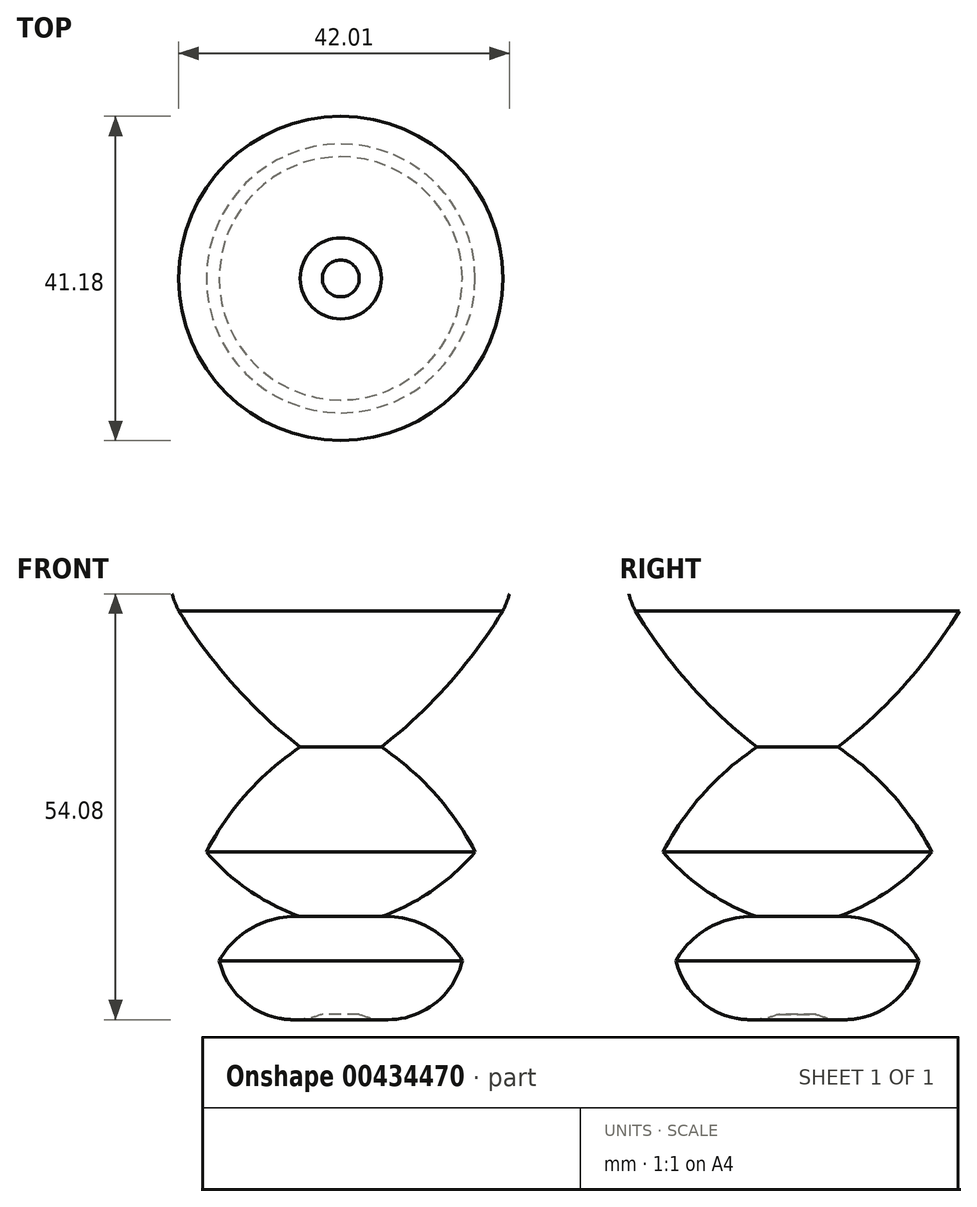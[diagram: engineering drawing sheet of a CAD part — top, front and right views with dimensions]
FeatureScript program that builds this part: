
annotation { "Feature Type Name" : "Feature", "Feature Type Description" : "" }
export const myFeature = defineFeature(function(context is Context, id is Id, definition is map)
    precondition{}
    {
        {
            var Q0;
            Q0=qCreatedBy(makeId("Front.planeOp"),FACE);
            var sketch = newSketch(context, id + "F0", { "sketchPlane" : qUnion([Q0])});
            skLineSegment(sketch, "E0", {"start": v(0, 0) * mm, "end": v(0, 68.09) * mm});
            skSolve(sketch);
        }
        {
            var Q0;
            Q0=qCreatedBy(makeId("Front.planeOp"),FACE);
            var sketch = newSketch(context, id + "F1", { "sketchPlane" : qUnion([Q0])});
            skArc(sketch, "E1", {"start": v(20.59, 51.23) * mm, "mid": v(14.7, 66.63) * mm, "end": v(0, 59.19) * mm});
            skArc(sketch, "E2", {"start": v(5.15, 33.92) * mm, "mid": v(13.64, 41.88) * mm, "end": v(20.59, 51.23) * mm});
            skArc(sketch, "E3", {"start": v(5.15, 12.4) * mm, "mid": v(11.65, 15.71) * mm, "end": v(17.08, 20.59) * mm});
            skArc(sketch, "E4", {"start": v(15.44, 6.78) * mm, "mid": v(11.1, 11.07) * mm, "end": v(5.15, 12.4) * mm});
            skArc(sketch, "E5", {"start": v(2.34, 0) * mm, "mid": v(10.45, 0.39) * mm, "end": v(15.44, 6.78) * mm});
            skArc(sketch, "E6", {"start": v(17.08, 20.59) * mm, "mid": v(11.96, 28.02) * mm, "end": v(5.15, 33.92) * mm});
            skSolve(sketch);
        }
        {
            var Q0;
            Q0=sQuery(id+"F1.wireOp",EDGE,"E1");
            var Q1;
            Q1=sQuery(id+"F1.wireOp",EDGE,"E4");
            var Q2;
            Q2=sQuery(id+"F1.wireOp",EDGE,"E5");
            var Q3;
            Q3=sQuery(id+"F1.wireOp",EDGE,"E3");
            var Q4;
            Q4=sQuery(id+"F1.wireOp",EDGE,"E2");
            var Q5;
            Q5=sQuery(id+"F1.wireOp",EDGE,"E6");
            var Q6;
            Q6=sQuery(id+"F0.wireOp",EDGE,"E0");
            revolve(context, id + "F2", {"bodyType" : ToolBodyType.SURFACE, "surfaceEntities" : qUnion([Q0, Q1, Q2, Q3, Q4, Q5]), "axis" : qUnion([Q6]), "revolveType" : RevolveType.FULL});
        }
    });
